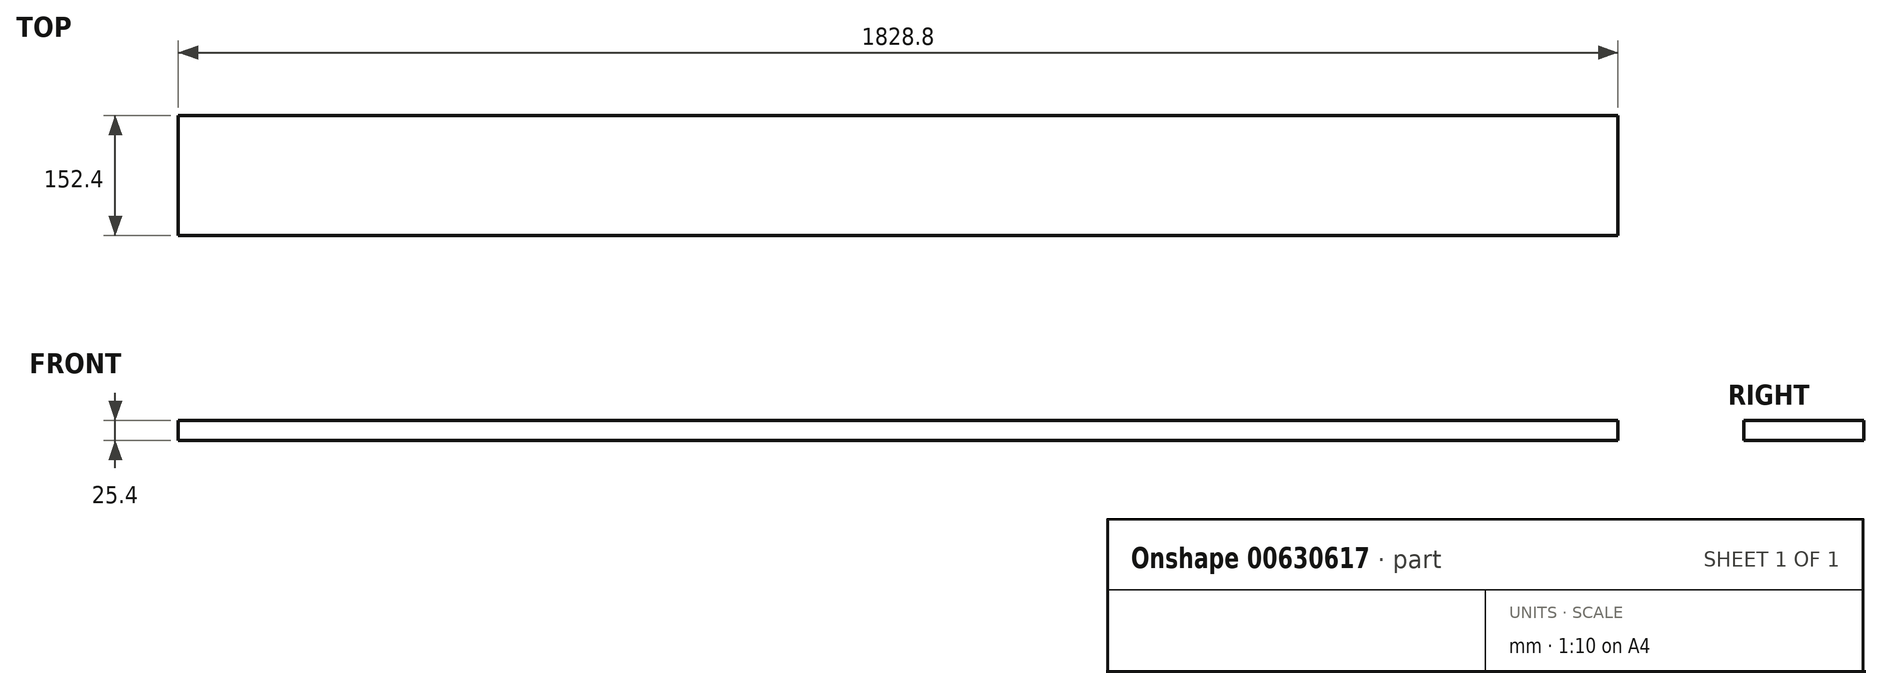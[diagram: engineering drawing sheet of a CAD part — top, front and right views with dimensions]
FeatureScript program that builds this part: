
annotation { "Feature Type Name" : "Feature", "Feature Type Description" : "" }
export const myFeature = defineFeature(function(context is Context, id is Id, definition is map)
    precondition{}
    {
        {
            var Q0;
            Q0=qCreatedBy(makeId("Right.planeOp"),FACE);
            var sketch = newSketch(context, id + "F0", { "sketchPlane" : qUnion([Q0])});
            skLineSegment(sketch, "E0.bottom", {"start": v(76.2, -12.7) * mm, "end": v(-76.2, -12.7) * mm});
            skLineSegment(sketch, "E0.top", {"start": v(76.2, 12.7) * mm, "end": v(-76.2, 12.7) * mm});
            skLineSegment(sketch, "E0.left", {"start": v(76.2, -12.7) * mm, "end": v(76.2, 12.7) * mm});
            skLineSegment(sketch, "E0.right", {"start": v(-76.2, -12.7) * mm, "end": v(-76.2, 12.7) * mm});
            skPoint(sketch, "E0.middle", {"position": v(0, 0) * mm});
            skSolve(sketch);
        }
        {
            var Q0;
            Q0 = qSketchRegion(id + "F0", true);
            extrude(context, id + "F1", {"entities" : qUnion([Q0]), "depth" : 1828.8 * mm, "offsetDistance" : 25.4 * mm});
        }
    });
